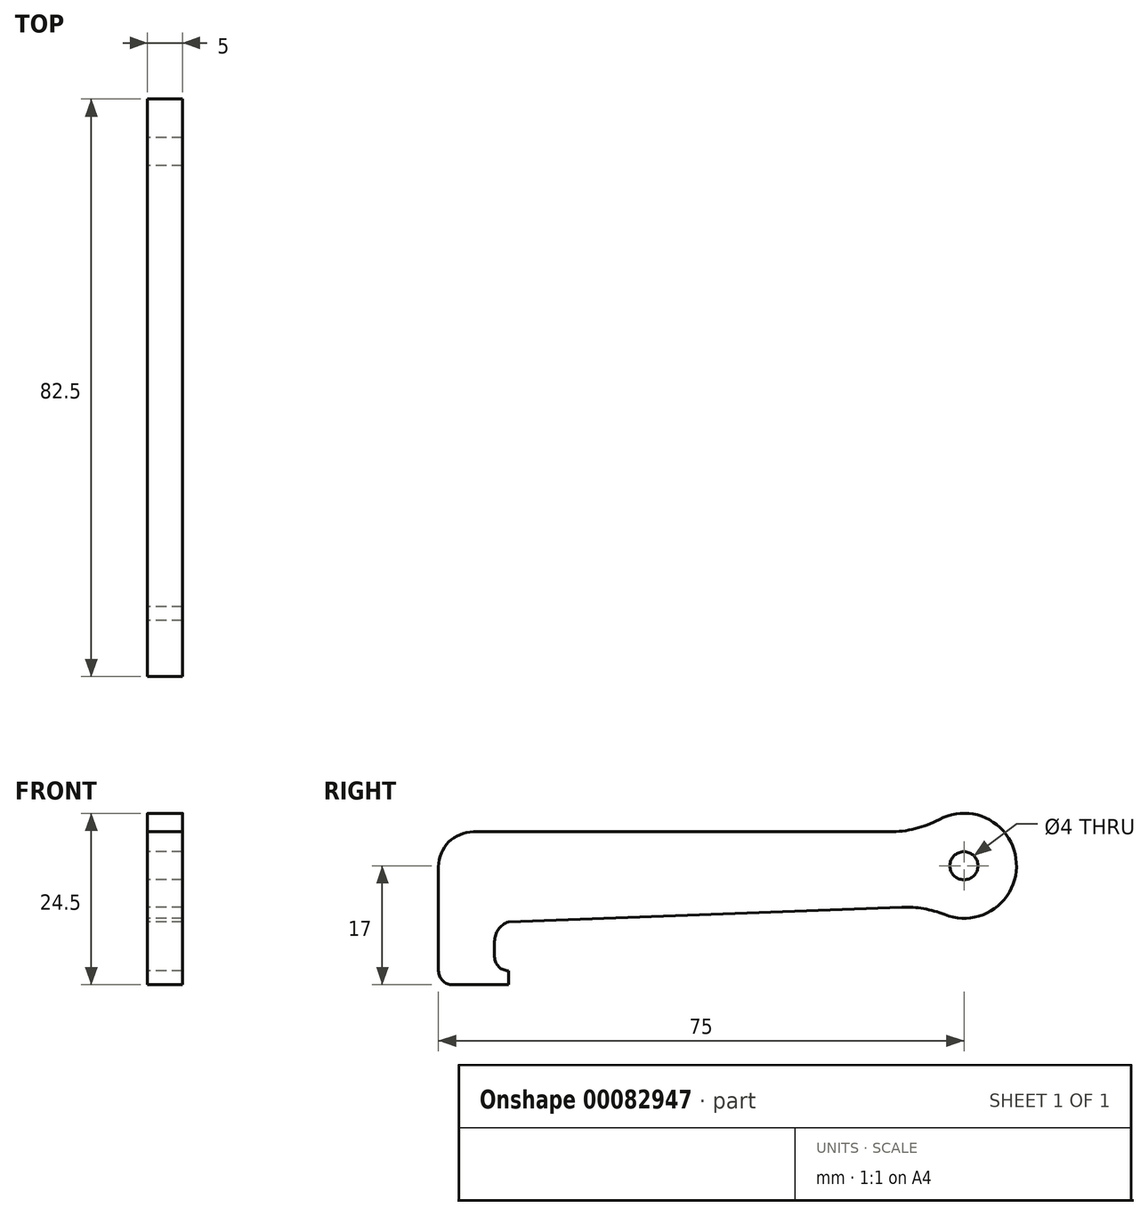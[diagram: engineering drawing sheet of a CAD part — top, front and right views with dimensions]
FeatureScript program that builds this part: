
annotation { "Feature Type Name" : "Feature", "Feature Type Description" : "" }
export const myFeature = defineFeature(function(context is Context, id is Id, definition is map)
    precondition{}
    {
        {
            var Q0;
            Q0=qCreatedBy(makeId("Right.planeOp"),FACE);
            var sketch = newSketch(context, id + "F0", { "sketchPlane" : qUnion([Q0])});
            skLineSegment(sketch, "E0", {"start": v(0, 0) * mm, "end": v(0, 2) * mm});
            skLineSegment(sketch, "E1", {"start": v(0, 2) * mm, "end": v(0, 2) * mm});
            skLineSegment(sketch, "E2", {"start": v(-2, 4) * mm, "end": v(-2, 6.17) * mm});
            skLineSegment(sketch, "E3", {"start": v(0, 0) * mm, "end": v(-8, 0) * mm});
            skLineSegment(sketch, "E4", {"start": v(-10, 2) * mm, "end": v(-10, 16.84) * mm});
            skLineSegment(sketch, "E5", {"start": v(-5, 21.84) * mm, "end": v(54.4, 21.84) * mm});
            skLineSegment(sketch, "E6", {"start": v(59.27, 38.41) * mm, "end": v(59.27, -12.96) * mm, "construction": true});
            skCircle(sketch, "E7", {"center": v(65, 17) * mm, "radius": 2 * mm});
            skArc(sketch, "E8", {"start": v(62.23, 10.03) * mm, "mid": v(72.49, 17.42) * mm, "end": v(61.46, 23.61) * mm});
            skPoint(sketch, "E9.visualSharp", {"position": v(59.27, 21.84) * mm});
            skArc(sketch, "E9.filletArc", {"start": v(54.4, 21.84) * mm, "mid": v(58.04, 22.3) * mm, "end": v(61.46, 23.61) * mm});
            skPoint(sketch, "E10.visualSharp", {"position": v(59.27, 12.16) * mm});
            skArc(sketch, "E10.filletArc", {"start": v(62.23, 10.03) * mm, "mid": v(59.24, 10.87) * mm, "end": v(56.15, 11.08) * mm});
            skArc(sketch, "E11.filletArc", {"start": v(0, 9) * mm, "mid": v(-1.45, 7.9) * mm, "end": v(-2, 6.17) * mm});
            skPoint(sketch, "E12.visualSharp", {"position": v(-2, 2) * mm});
            skArc(sketch, "E12.filletArc", {"start": v(-2, 4) * mm, "mid": v(-1.41, 2.59) * mm, "end": v(0, 2) * mm});
            skPoint(sketch, "E13.visualSharp", {"position": v(-10, 0) * mm});
            skArc(sketch, "E13.filletArc", {"start": v(-10, 2) * mm, "mid": v(-9.41, 0.59) * mm, "end": v(-8, 0) * mm});
            skLineSegment(sketch, "E14", {"start": v(0, 9) * mm, "end": v(56.15, 11.08) * mm});
            skArc(sketch, "E15.filletArc", {"start": v(-5, 21.84) * mm, "mid": v(-8.54, 20.38) * mm, "end": v(-10, 16.84) * mm});
            skSolve(sketch);
        }
        {
            var Q0;
            Q0=makeQuery(id+"F0.imprint","IMPRINT",FACE,{"disambiguationData":[TD([[makeQuery(id+"F0.imprint","IMPRINT",EDGE,{"derivedFrom":sQuery(id+"F0.wireOp",EDGE,"E0")}),1.0]])]});
            extrude(context, id + "F1", {"entities" : qUnion([Q0]), "depth" : 5 * mm});
        }
    });
